# Revit family: Electrical_Equipment-Floor_Box-Hubbell_Wiring-2_Gang-Concrete_Shallow-CFB2G25R
name_source: partatom
category: Electrical Fixtures
revit_build: Autodesk Revit 2015 (Build: 20140606_1530(x64)
units: mm (PartAtom-declared; Revit-internal decimal feet)

## types (2) — shared parameters
Assembly Code = D5020115
Conduit Connector 1 Radius = 0.5 "
Conduit Connector_1 Description = Conduit 1in. 0.75in. or 0.5in. Connection
Conduit Connector_10 Description = Conduit 1in. 0.75in. or 0.5in. Connection
Conduit Connector_2 Description = Conduit 1in. 0.75in. or 0.5in. Connection
Conduit Connector_3 Description = Conduit 1in. 0.75in. or 0.5in. Connection
Conduit Connector_4 Description = Conduit 1in. 0.75in. or 0.5in. Connection
Conduit Connector_5 Description = Conduit 1in. 0.75in. or 0.5in. Connection
Conduit Connector_6 Description = Conduit 1in. 0.75in. or 0.5in. Connection
Conduit Connector_7 Description = Conduit 1in. 0.75in. or 0.5in. Connection
Conduit Connector_8 Description = Conduit 1in. 0.75in. or 0.5in. Connection
Conduit Connector_9 Description = Conduit 1in. 0.75in. or 0.5in. Connection
Description = Concrete Floor Box, 2 Gang for 6in Round Cover Shallow
Manufacturer = Hubbell-Wiring
Product Documentation Link = http://www.hubbell-wiring.com
Product Page URL = http://ecatalog.hubbell-wiring.com
Product data url = https://bimobject.com
URL = http://www.hubbell-wiring.com
zero-valued in all types: Default Elevation

## per-type parameters (varying)
| type | Box Material |
| CFB2G25R | Metal - Hubbell - Steel |
| CFB2G25RCR | Metal - Hubbell - Green Finish |

note: column(s) folded — value = type name in every type: Model

## geometry (parser evidence)
native form markers: Blend x20, Revolve x1, Sweep x7
no freeform markers — native parametric forms only
